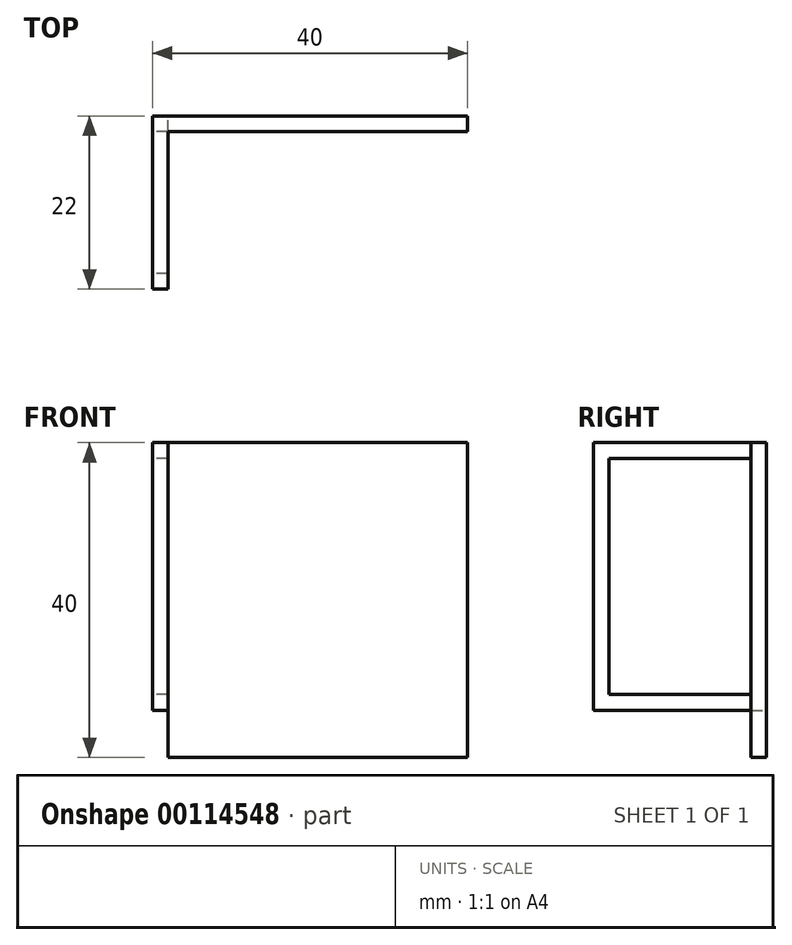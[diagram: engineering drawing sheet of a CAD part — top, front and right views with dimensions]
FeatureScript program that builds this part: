
annotation { "Feature Type Name" : "Feature", "Feature Type Description" : "" }
export const myFeature = defineFeature(function(context is Context, id is Id, definition is map)
    precondition{}
    {
        {
            var Q0;
            Q0=qCreatedBy(makeId("Front.planeOp"),FACE);
            var sketch = newSketch(context, id + "F0", { "sketchPlane" : qUnion([Q0])});
            skLineSegment(sketch, "E0.bottom", {"start": v(-51.1, 5.4) * mm, "end": v(-11.1, 5.4) * mm});
            skLineSegment(sketch, "E0.top", {"start": v(-51.1, 45.4) * mm, "end": v(-11.1, 45.4) * mm});
            skLineSegment(sketch, "E0.left", {"start": v(-51.1, 45.4) * mm, "end": v(-51.1, 5.4) * mm});
            skLineSegment(sketch, "E0.right", {"start": v(-11.1, 45.4) * mm, "end": v(-11.1, 5.4) * mm});
            skSolve(sketch);
        }
        {
            var Q0;
            Q0=makeQuery(id+"F0.imprint","IMPRINT",FACE,{"disambiguationData":[TD([[makeQuery(id+"F0.imprint","IMPRINT",EDGE,{"derivedFrom":sQuery(id+"F0.wireOp",EDGE,"E0.bottom")}),1.0]])]});
            extrude(context, id + "F1", {"entities" : qUnion([Q0]), "depth" : 2 * mm});
        }
        {
            var Q0;
            Q0=makeQuery(id+"F1.opExtrude","CAP_FACE",FACE,{"disambiguationData":[OSD([sQuery(id+"F0.wireOp",EDGE,"E0.bottom"),sQuery(id+"F0.wireOp",EDGE,"E0.top"),sQuery(id+"F0.wireOp",EDGE,"E0.left"),sQuery(id+"F0.wireOp",EDGE,"E0.right")])],"isStart":false});
            var sketch = newSketch(context, id + "F2", { "sketchPlane" : qUnion([Q0])});
            skLineSegment(sketch, "E1", {"start": v(-51.1, 45.4) * mm, "end": v(-49.1, 45.4) * mm});
            skLineSegment(sketch, "E2", {"start": v(-49.1, 45.4) * mm, "end": v(-49.1, 11.4) * mm});
            skLineSegment(sketch, "E3", {"start": v(-49.1, 11.4) * mm, "end": v(-51.1, 11.4) * mm});
            skLineSegment(sketch, "E4", {"start": v(-51.1, 11.4) * mm, "end": v(-51.1, 45.4) * mm});
            skSolve(sketch);
        }
        {
            var Q0;
            Q0=qSketchRegion(id+"F2",true);
            extrude(context, id + "F3", {"entities" : qUnion([Q0]), "operationType" : NewBodyOperationType.ADD, "depth" : 20 * mm});
        }
        {
            var Q0;
            Q0=makeQuery(id+"F3.boolean.opBoolean","MERGE",FACE,{"derivedFrom":[makeQuery(id+"F1.opExtrude","SWEPT_FACE",FACE,{"disambiguationData":[OSD([sQuery(id+"F0.wireOp",EDGE,"E0.left")])]}),makeQuery(id+"F3.opExtrude","SWEPT_FACE",FACE,{"disambiguationData":[OSD([sQuery(id+"F2.wireOp",EDGE,"c9865763-67e1-455c-a659-3f5a931a98e0.0")])]})]});
            var sketch = newSketch(context, id + "F4", { "sketchPlane" : qUnion([Q0])});
            skLineSegment(sketch, "E5.bottom", {"start": v(2, 43.4) * mm, "end": v(20, 43.4) * mm});
            skLineSegment(sketch, "E5.top", {"start": v(2, 13.4) * mm, "end": v(20, 13.4) * mm});
            skLineSegment(sketch, "E5.left", {"start": v(2, 43.4) * mm, "end": v(2, 13.4) * mm});
            skLineSegment(sketch, "E5.right", {"start": v(20, 43.4) * mm, "end": v(20, 13.4) * mm});
            skSolve(sketch);
        }
        {
            var Q0;
            Q0=qSketchRegion(id+"F4",true);
            extrude(context, id + "F5", {"entities" : qUnion([Q0]), "operationType" : NewBodyOperationType.REMOVE, "endBound" : BoundingType.THROUGH_ALL, "oppositeDirection" : true, "depth" : 25 * mm});
        }
        {
            var Q0;
            Q0=makeQuery(id+"F3.boolean.opBoolean","MERGE",FACE,{"derivedFrom":[makeQuery(id+"F1.opExtrude","SWEPT_FACE",FACE,{"disambiguationData":[OSD([sQuery(id+"F0.wireOp",EDGE,"E0.left")])]}),makeQuery(id+"F3.opExtrude","SWEPT_FACE",FACE,{"disambiguationData":[OSD([sQuery(id+"F2.wireOp",EDGE,"E4")])]})]});
            var sketch = newSketch(context, id + "F6", { "sketchPlane" : qUnion([Q0])});
            skLineSegment(sketch, "E6.0", {"start": v(2, 5.4) * mm, "end": v(0, 5.4) * mm});
            skLineSegment(sketch, "E6.1", {"start": v(2, 11.4) * mm, "end": v(2, 5.4) * mm});
            skLineSegment(sketch, "E7", {"start": v(2, 11.4) * mm, "end": v(0, 11.4) * mm});
            skLineSegment(sketch, "E8", {"start": v(0, 11.4) * mm, "end": v(0, 5.4) * mm});
            skSolve(sketch);
        }
        {
            var Q0;
            Q0=qSketchRegion(id+"F6",true);
            extrude(context, id + "F7", {"entities" : qUnion([Q0]), "operationType" : NewBodyOperationType.REMOVE, "oppositeDirection" : true, "depth" : 2 * mm});
        }
        {
            var Q0;
            Q0=qCreatedBy(makeId("Front.planeOp"),FACE);
            var sketch = newSketch(context, id + "F8", { "sketchPlane" : qUnion([Q0])});
            skLineSegment(sketch, "E9", {"start": v(-119.27, 20.28) * mm, "end": v(-106.52, 6.34) * mm});
            skLineSegment(sketch, "E10", {"start": v(-106.52, 6.34) * mm, "end": v(-86.1, 6.34) * mm});
            skSolve(sketch);
        }
        {
            var Q0;
            Q0=qSketchRegion(id+"F8",true);
            var Q1;
            Q1=sQuery(id+"F8.wireOp",EDGE,"E9");
            extrude(context, id + "F9", {"entities" : qUnion([Q0]), "bodyType" : ToolBodyType.SURFACE, "surfaceEntities" : qUnion([Q1]), "depth" : 25 * mm});
        }
    });
